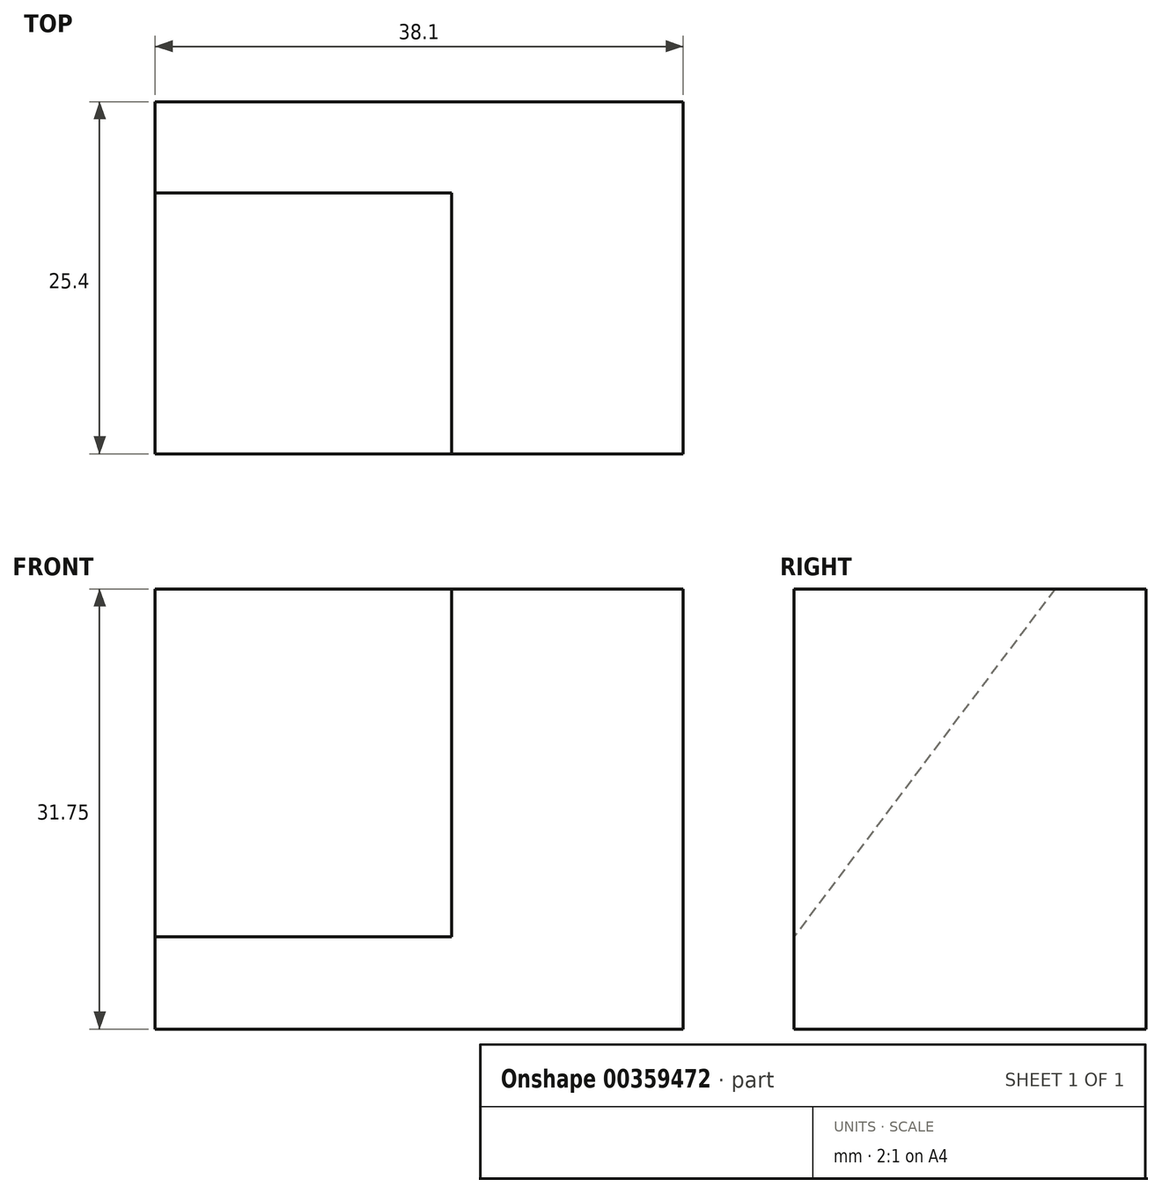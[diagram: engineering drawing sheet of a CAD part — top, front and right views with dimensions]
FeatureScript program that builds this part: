
annotation { "Feature Type Name" : "Feature", "Feature Type Description" : "" }
export const myFeature = defineFeature(function(context is Context, id is Id, definition is map)
    precondition{}
    {
        {
            var Q0;
            Q0=qCreatedBy(makeId("Front.planeOp"),FACE);
            var sketch = newSketch(context, id + "F0", { "sketchPlane" : qUnion([Q0])});
            skLineSegment(sketch, "E0", {"start": v(4, 41.12) * mm, "end": v(4, 9.37) * mm});
            skLineSegment(sketch, "E1", {"start": v(4, 9.37) * mm, "end": v(42.1, 9.37) * mm});
            skLineSegment(sketch, "E2", {"start": v(42.1, 9.37) * mm, "end": v(42.1, 41.12) * mm});
            skLineSegment(sketch, "E3", {"start": v(42.1, 41.12) * mm, "end": v(4, 41.12) * mm});
            skSolve(sketch);
        }
        {
            var Q0;
            Q0=makeQuery(id+"F0.imprint","IMPRINT",FACE,{"disambiguationData":[TD([[makeQuery(id+"F0.imprint","IMPRINT",EDGE,{"derivedFrom":sQuery(id+"F0.wireOp",EDGE,"E0")}),1.0]])]});
            extrude(context, id + "F1", {"entities" : qUnion([Q0]), "depth" : 25.4 * mm});
        }
        {
            var Q0;
            Q0=qCreatedBy(makeId("Right.planeOp"),FACE);
            var sketch = newSketch(context, id + "F2", { "sketchPlane" : qUnion([Q0])});
            skLineSegment(sketch, "E4", {"start": v(-25.47, 15.93) * mm, "end": v(-6.42, 41.33) * mm});
            skLineSegment(sketch, "E5", {"start": v(-6.42, 41.33) * mm, "end": v(-25.47, 41.33) * mm});
            skLineSegment(sketch, "E6", {"start": v(-25.47, 41.33) * mm, "end": v(-25.47, 15.93) * mm});
            skSolve(sketch);
        }
        {
            var Q0;
            Q0 = qSketchRegion(id + "F2", true);
            var Q1;
            Q1=makeQuery(id+"F1.opExtrude","SWEPT_FACE",FACE,{"disambiguationData":[OSD([sQuery(id+"F0.wireOp",EDGE,"E2")])]});
            extrude(context, id + "F3", {"entities" : qUnion([Q0, Q1]), "operationType" : NewBodyOperationType.REMOVE, "depth" : 25.4 * mm});
        }
    });
